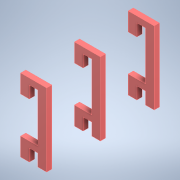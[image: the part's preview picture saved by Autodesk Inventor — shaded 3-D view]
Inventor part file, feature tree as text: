
AUTODESK INVENTOR PART (.ipt)
format: ipt  version: 2021 (Build 250183000, 183)  size: 163,328 bytes
history: native  units: in
note: dims shown in document units (in); Inventor stores cm internally (conversion verified against a paired STEP export)
features: plane x2, mirror x2, extrude x1, sketch x1
ambient origin geometry x8: Origin, YZ Plane, XZ Plane, XY Plane, X Axis, Y Axis, Z Axis, Center Point
bodies: Solid1 (feature_tree)
feature tree (6):
  extrude  "Extrusion1"  Depth=0.175in
  plane  "Work Plane2"
  plane  "Work Plane3"
  mirror  "Mirror2"
  mirror  "Mirror3"
  sketch  "Sketch1"  dims[d1=1.4in d2=0.175in d3=0.175in d4=0.25in d6=0.25in d7=0.25in d11=0.15in d12=0.0in d13=0.525in d14=0.525in d16=0.775in d17=-0.775in]
